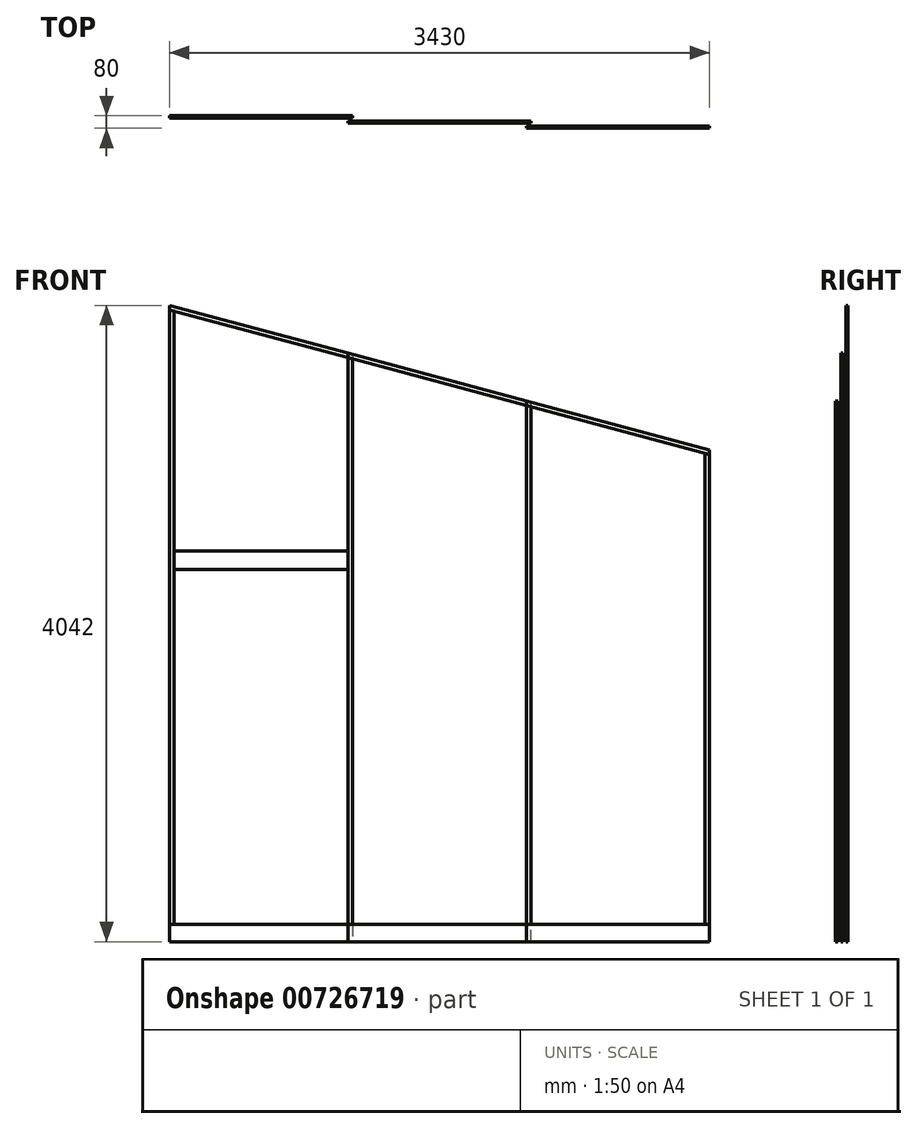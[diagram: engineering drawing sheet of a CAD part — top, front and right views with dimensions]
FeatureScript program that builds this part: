
annotation { "Feature Type Name" : "Feature", "Feature Type Description" : "" }
export const myFeature = defineFeature(function(context is Context, id is Id, definition is map)
    precondition{}
    {
        {
            assignVariable(context, id + "F0", {"name" : "bredd", "anyValue" : 28});
        }
        {
            var Q0;
            Q0=qCreatedBy(makeId("Front.planeOp"),FACE);
            var sketch = newSketch(context, id + "F1", { "sketchPlane" : qUnion([Q0])});
            skLineSegment(sketch, "E0", {"start": v(0, 0) * mm, "end": v(8388.04, 0) * mm});
            skLineSegment(sketch, "E1", {"start": v(8388.04, 0) * mm, "end": v(8388.04, 3249.78) * mm});
            skLineSegment(sketch, "E2", {"start": v(8388.04, 3249.78) * mm, "end": v(0, 5470.3) * mm});
            skLineSegment(sketch, "E3", {"start": v(0, 5470.3) * mm, "end": v(0, 0) * mm});
            skLineSegment(sketch, "E4", {"start": v(1277.9, 5132) * mm, "end": v(1277.9, 0) * mm, "construction": true});
            skLineSegment(sketch, "E5", {"start": v(4707.9, 4224) * mm, "end": v(4707.9, 0) * mm, "construction": true});
            skLineSegment(sketch, "E6", {"start": v(1277.9, 4042) * mm, "end": v(4707.9, 3124) * mm, "construction": true});
            skLineSegment(sketch, "E7", {"start": v(5395.42, 4042) * mm, "end": v(5395.42, 0) * mm, "construction": true});
            skSolve(sketch);
        }
        {
            var Q0;
            Q0=qCreatedBy(makeId("Front.planeOp"),FACE);
            var sketch = newSketch(context, id + "F2", { "sketchPlane" : qUnion([Q0])});
            skLineSegment(sketch, "E8.bottom", {"start": v(1277.9, 0) * mm, "end": v(1372.9, 0) * mm});
            skLineSegment(sketch, "E8.top", {"start": v(1277.9, 2328) * mm, "end": v(1372.9, 2328) * mm});
            skLineSegment(sketch, "E8.left", {"start": v(1277.9, 0) * mm, "end": v(1277.9, 2328) * mm});
            skLineSegment(sketch, "E8.right", {"start": v(1372.9, 0) * mm, "end": v(1372.9, 2328) * mm});
            skLineSegment(sketch, "E9.bottom", {"start": v(2372.9, 0) * mm, "end": v(2492.9, 0) * mm});
            skLineSegment(sketch, "E9.top", {"start": v(2372.9, 2328) * mm, "end": v(2492.9, 2328) * mm});
            skLineSegment(sketch, "E9.left", {"start": v(2372.9, 0) * mm, "end": v(2372.9, 2328) * mm});
            skLineSegment(sketch, "E9.right", {"start": v(2492.9, 0) * mm, "end": v(2492.9, 2328) * mm});
            skLineSegment(sketch, "E10.bottom", {"start": v(3492.9, 0) * mm, "end": v(3612.9, 0) * mm});
            skLineSegment(sketch, "E10.top", {"start": v(3492.9, 2328) * mm, "end": v(3612.9, 2328) * mm});
            skLineSegment(sketch, "E10.left", {"start": v(3492.9, 0) * mm, "end": v(3492.9, 2328) * mm});
            skLineSegment(sketch, "E10.right", {"start": v(3612.9, 0) * mm, "end": v(3612.9, 2328) * mm});
            skLineSegment(sketch, "E11", {"start": v(1277.9, 2328) * mm, "end": v(4707.9, 2328) * mm, "construction": true});
            skLineSegment(sketch, "E12.bottom", {"start": v(4707.9, 2328) * mm, "end": v(4612.9, 2328) * mm});
            skLineSegment(sketch, "E12.top", {"start": v(4707.9, 0) * mm, "end": v(4612.9, 0) * mm});
            skLineSegment(sketch, "E12.left", {"start": v(4707.9, 2328) * mm, "end": v(4707.9, 0) * mm});
            skLineSegment(sketch, "E12.right", {"start": v(4612.9, 2328) * mm, "end": v(4612.9, 0) * mm});
            skLineSegment(sketch, "E13.bottom", {"start": v(1262.9, 2328) * mm, "end": v(4722.9, 2328) * mm});
            skLineSegment(sketch, "E13.top", {"start": v(1262.9, 2423) * mm, "end": v(4722.9, 2423) * mm});
            skLineSegment(sketch, "E13.left", {"start": v(1262.9, 2328) * mm, "end": v(1262.9, 2423) * mm});
            skLineSegment(sketch, "E13.right", {"start": v(4722.9, 2328) * mm, "end": v(4722.9, 2423) * mm});
            skLineSegment(sketch, "E14.0", {"start": v(1277.9, 4042) * mm, "end": v(4707.9, 3124) * mm, "construction": true});
            skLineSegment(sketch, "E15", {"start": v(1262.9, 4046.01) * mm, "end": v(4722.9, 3119.99) * mm});
            skLineSegment(sketch, "E16", {"start": v(4722.9, 3119.99) * mm, "end": v(4722.9, 3021.64) * mm});
            skLineSegment(sketch, "E17", {"start": v(4722.9, 3021.64) * mm, "end": v(1262.9, 3947.67) * mm});
            skLineSegment(sketch, "E18", {"start": v(1262.9, 4046.01) * mm, "end": v(1262.9, 3947.67) * mm});
            skLineSegment(sketch, "E19", {"start": v(1262.9, 2423) * mm, "end": v(1262.9, 4046.01) * mm, "construction": true});
            skLineSegment(sketch, "E20", {"start": v(4722.9, 2423) * mm, "end": v(4722.9, 3119.99) * mm, "construction": true});
            skLineSegment(sketch, "E21.bottom", {"start": v(1277.9, 2483) * mm, "end": v(1372.9, 2483) * mm});
            skLineSegment(sketch, "E21.left", {"start": v(1277.9, 2483) * mm, "end": v(1277.9, 3943.66) * mm});
            skLineSegment(sketch, "E21.right", {"start": v(1372.9, 2483) * mm, "end": v(1372.9, 3918.23) * mm});
            skLineSegment(sketch, "E22.bottom", {"start": v(2372.9, 2483) * mm, "end": v(2492.9, 2483) * mm});
            skLineSegment(sketch, "E22.left", {"start": v(2372.9, 2483) * mm, "end": v(2372.9, 3650.6) * mm});
            skLineSegment(sketch, "E22.right", {"start": v(2492.9, 2483) * mm, "end": v(2492.9, 3618.48) * mm});
            skLineSegment(sketch, "E23.bottom", {"start": v(3492.9, 2483) * mm, "end": v(3612.9, 2483) * mm});
            skLineSegment(sketch, "E23.left", {"start": v(3492.9, 2483) * mm, "end": v(3492.9, 3350.84) * mm});
            skLineSegment(sketch, "E23.right", {"start": v(3612.9, 2483) * mm, "end": v(3612.9, 3318.72) * mm});
            skLineSegment(sketch, "E24.bottom", {"start": v(4612.9, 2483) * mm, "end": v(4707.9, 2483) * mm});
            skLineSegment(sketch, "E24.left", {"start": v(4612.9, 2483) * mm, "end": v(4612.9, 3051.08) * mm});
            skLineSegment(sketch, "E24.right", {"start": v(4707.9, 2483) * mm, "end": v(4707.9, 3025.66) * mm});
            skPoint(sketch, "E25.orphan", {"position": v(3612.9, 2483) * mm});
            skPoint(sketch, "E26.orphan", {"position": v(2492.9, 3618.48) * mm});
            skPoint(sketch, "E27.orphan", {"position": v(1372.9, 3918.23) * mm});
            skLineSegment(sketch, "E28", {"start": v(1372.9, 2571) * mm, "end": v(2372.9, 2571) * mm});
            skLineSegment(sketch, "E29", {"start": v(2492.9, 2571) * mm, "end": v(3492.9, 2571) * mm});
            skLineSegment(sketch, "E30", {"start": v(3612.9, 2571) * mm, "end": v(4612.9, 2571) * mm});
            skLineSegment(sketch, "E31", {"start": v(4612.9, 2498) * mm, "end": v(3612.9, 2498) * mm});
            skLineSegment(sketch, "E32", {"start": v(3492.9, 2498) * mm, "end": v(2492.9, 2498) * mm});
            skLineSegment(sketch, "E33", {"start": v(2372.9, 2498) * mm, "end": v(1372.9, 2498) * mm});
            skSolve(sketch);
        }
        {
            var Q0;
            Q0=qCreatedBy(makeId("Front.planeOp"),FACE);
            var sketch = newSketch(context, id + "F3", { "sketchPlane" : qUnion([Q0])});
            skPoint(sketch, "E34.0", {"position": v(1277.9, 0) * mm});
            skPoint(sketch, "E35.0", {"position": v(4707.9, 0) * mm});
            skPoint(sketch, "E36.0", {"position": v(4707.9, 3124) * mm});
            skPoint(sketch, "E37.0", {"position": v(1277.9, 4042) * mm});
            skLineSegment(sketch, "E38", {"start": v(1277.9, 0) * mm, "end": v(1277.9, 4042) * mm});
            skLineSegment(sketch, "E39", {"start": v(4707.9, 0) * mm, "end": v(4707.9, 3124) * mm});
            skLineSegment(sketch, "E40", {"start": v(1277.9, 0) * mm, "end": v(4707.9, 0) * mm, "construction": true});
            skLineSegment(sketch, "E41", {"start": v(2411.9, 110) * mm, "end": v(2411.9, 3709.51) * mm});
            skLineSegment(sketch, "E42", {"start": v(2439.9, 3731) * mm, "end": v(2439.9, 0) * mm});
            skLineSegment(sketch, "E43", {"start": v(3545.9, 3435) * mm, "end": v(3545.9, 0) * mm});
            skLineSegment(sketch, "E44", {"start": v(3573.9, 110) * mm, "end": v(3573.9, 3398.52) * mm});
            skLineSegment(sketch, "E45", {"start": v(2411.9, 0) * mm, "end": v(2439.9, 0) * mm});
            skLineSegment(sketch, "E46.bottom", {"start": v(1277.9, -203.85) * mm, "end": v(2439.9, -203.85) * mm, "construction": true});
            skLineSegment(sketch, "E46.top", {"start": v(1277.9, -239.4) * mm, "end": v(2439.9, -239.4) * mm, "construction": true});
            skLineSegment(sketch, "E46.left", {"start": v(1277.9, -203.85) * mm, "end": v(1277.9, -239.4) * mm, "construction": true});
            skLineSegment(sketch, "E46.right", {"start": v(2439.9, -203.85) * mm, "end": v(2439.9, -239.4) * mm, "construction": true});
            skLineSegment(sketch, "E47.bottom", {"start": v(2411.9, -167.17) * mm, "end": v(3573.9, -167.17) * mm, "construction": true});
            skLineSegment(sketch, "E47.top", {"start": v(2411.9, -203.85) * mm, "end": v(3573.9, -203.85) * mm, "construction": true});
            skLineSegment(sketch, "E47.left", {"start": v(2411.9, -167.17) * mm, "end": v(2411.9, -203.85) * mm, "construction": true});
            skLineSegment(sketch, "E47.right", {"start": v(3573.9, -167.17) * mm, "end": v(3573.9, -203.85) * mm, "construction": true});
            skLineSegment(sketch, "E48.bottom", {"start": v(4707.9, -203.85) * mm, "end": v(3545.9, -203.85) * mm, "construction": true});
            skLineSegment(sketch, "E48.top", {"start": v(4707.9, -239.4) * mm, "end": v(3545.9, -239.4) * mm, "construction": true});
            skLineSegment(sketch, "E48.left", {"start": v(4707.9, -203.85) * mm, "end": v(4707.9, -239.4) * mm, "construction": true});
            skLineSegment(sketch, "E48.right", {"start": v(3545.9, -203.85) * mm, "end": v(3545.9, -239.4) * mm, "construction": true});
            skLineSegment(sketch, "E49.0", {"start": v(1305.9, 110) * mm, "end": v(1305.9, 4005.52) * mm});
            skLineSegment(sketch, "E50.0", {"start": v(4679.9, 110) * mm, "end": v(4679.9, 3102.5) * mm});
            skLineSegment(sketch, "E51", {"start": v(4707.9, 3124) * mm, "end": v(3545.9, 3435) * mm});
            skLineSegment(sketch, "E52", {"start": v(1277.9, 4042) * mm, "end": v(2439.9, 3731) * mm});
            skLineSegment(sketch, "E53.0", {"start": v(1277.9, 4013.01) * mm, "end": v(2439.9, 3702.02) * mm});
            skLineSegment(sketch, "E54.0", {"start": v(4707.9, 3095.01) * mm, "end": v(3545.9, 3406.01) * mm});
            skLineSegment(sketch, "E55", {"start": v(1277.9, 4042) * mm, "end": v(4707.9, 3124) * mm, "construction": true});
            skLineSegment(sketch, "E56", {"start": v(1277.9, 0) * mm, "end": v(2439.9, 0) * mm});
            skLineSegment(sketch, "E57", {"start": v(2439.9, 110) * mm, "end": v(1277.9, 110) * mm});
            skLineSegment(sketch, "E58", {"start": v(3545.9, 0) * mm, "end": v(4707.9, 0) * mm});
            skLineSegment(sketch, "E59", {"start": v(3545.9, 110) * mm, "end": v(4707.9, 110) * mm});
            skPoint(sketch, "E60.orphan", {"position": v(3573.9, 0) * mm});
            skLineSegment(sketch, "E61.bottom", {"start": v(1305.9, 2483.58) * mm, "end": v(2411.9, 2483.58) * mm});
            skLineSegment(sketch, "E61.top", {"start": v(1305.9, 2363.58) * mm, "end": v(2411.9, 2363.58) * mm});
            skLineSegment(sketch, "E61.left", {"start": v(1305.9, 2483.58) * mm, "end": v(1305.9, 2363.58) * mm});
            skLineSegment(sketch, "E61.right", {"start": v(2411.9, 2483.58) * mm, "end": v(2411.9, 2363.58) * mm});
            skSolve(sketch);
        }
        {
            var Q0;
            Q0=qCreatedBy(makeId("Front.planeOp"),FACE);
            var sketch = newSketch(context, id + "F4", { "sketchPlane" : qUnion([Q0])});
            skLineSegment(sketch, "E62.0", {"start": v(2411.9, 110) * mm, "end": v(2411.9, 3709.51) * mm});
            skLineSegment(sketch, "E63.0", {"start": v(3573.9, 110) * mm, "end": v(3573.9, 3398.52) * mm});
            skLineSegment(sketch, "E64", {"start": v(2411.9, 110) * mm, "end": v(3573.9, 110) * mm});
            skLineSegment(sketch, "E65", {"start": v(3573.9, 3398.52) * mm, "end": v(2411.9, 3709.51) * mm});
            skLineSegment(sketch, "E66.0", {"start": v(3545.9, 110) * mm, "end": v(3545.9, 3406.01) * mm});
            skLineSegment(sketch, "E66.2", {"start": v(2439.9, 110) * mm, "end": v(2439.9, 3702.02) * mm});
            skLineSegment(sketch, "E67", {"start": v(2411.9, 110) * mm, "end": v(2411.9, 0) * mm});
            skLineSegment(sketch, "E68", {"start": v(2411.9, 0) * mm, "end": v(3573.9, 0) * mm});
            skLineSegment(sketch, "E69", {"start": v(3573.9, 0) * mm, "end": v(3573.9, 110) * mm});
            skLineSegment(sketch, "E70.0", {"start": v(3573.9, 3427.5) * mm, "end": v(2411.9, 3738.5) * mm});
            skLineSegment(sketch, "E71", {"start": v(3573.9, 3398.52) * mm, "end": v(3573.9, 3427.5) * mm});
            skLineSegment(sketch, "E72", {"start": v(2411.9, 3709.51) * mm, "end": v(2411.9, 3738.5) * mm});
            skSolve(sketch);
        }
        {
            var Q0;
            {var subQ4=sQuery(id+"F3.wireOp",EDGE,"E52");Q0=makeQuery(id+"F3.imprint","IMPRINT",FACE,{"disambiguationData":[TD([[makeQuery(id+"F3.imprint","IMPRINT",EDGE,{"derivedFrom":subQ4}),-1.0]])]});}
            extrude(context, id + "F5", {"entities" : qUnion([Q0]), "depth" : (getVariable(context, 'bredd') / 2) * mm, "offsetDistance" : 25 * mm});
        }
        {
            var Q0;
            {var subQ0=sQuery(id+"F3.wireOp",EDGE,"E41");Q0=makeQuery(id+"F3.imprint","IMPRINT",FACE,{"disambiguationData":[TD([[makeQuery(id+"F3.imprint","IMPRINT",EDGE,{"derivedFrom":subQ0}),-1.0]])]});}
            extrude(context, id + "F6", {"entities" : qUnion([Q0]), "depth" : (getVariable(context, 'bredd') / 2) * mm, "offsetDistance" : 25 * mm});
        }
        {
            var Q0;
            {var subQ5=sQuery(id+"F3.wireOp",EDGE,"E49.0");Q0=makeQuery(id+"F3.imprint","IMPRINT",FACE,{"disambiguationData":[TD([[makeQuery(id+"F3.imprint","IMPRINT",EDGE,{"derivedFrom":subQ5}),1.0]])]});}
            extrude(context, id + "F7", {"entities" : qUnion([Q0]), "depth" : (getVariable(context, 'bredd') / 2) * mm, "offsetDistance" : 25 * mm});
        }
        {
            var Q0;
            {var subQ0=sQuery(id+"F3.wireOp",EDGE,"E56");var subQ1=sQuery(id+"F3.wireOp",EDGE,"E38");var subQ2=makeQuery(id+"F3.imprint","INTERSECT",VERTEX,{"derivedFrom":[subQ1,subQ0]});Q0=makeQuery(id+"F3.imprint","IMPRINT",FACE,{"disambiguationData":[TD([[makeQuery(id+"F3.imprint","IMPRINT",EDGE,{"disambiguationData":[TD([[subQ2,-1.0]])],"derivedFrom":subQ1}),-1.0]])]});}
            extrude(context, id + "F8", {"entities" : qUnion([Q0]), "depth" : (getVariable(context, 'bredd') / 2) * mm, "offsetDistance" : 25 * mm});
        }
        {
            var Q0;
            Q0=makeQuery(id+"F4.imprint","IMPRINT",FACE,{"disambiguationData":[TD([[makeQuery(id+"F4.imprint","IMPRINT",EDGE,{"derivedFrom":sQuery(id+"F4.wireOp",EDGE,"E70.0")}),1.0]])]});
            extrude(context, id + "F9", {"entities" : qUnion([Q0]), "depth" : (getVariable(context, 'bredd') + 5 + getVariable(context, 'bredd') / 2) * mm, "offsetDistance" : 25 * mm, "hasSecondDirection" : true, "secondDirectionOppositeDirection" : false, "secondDirectionDepth" : (getVariable(context, 'bredd') + 5) * mm});
        }
        {
            var Q0;
            {var subQ0=sQuery(id+"F4.wireOp",EDGE,"E62.0");Q0=makeQuery(id+"F4.imprint","IMPRINT",FACE,{"disambiguationData":[TD([[makeQuery(id+"F4.imprint","IMPRINT",EDGE,{"derivedFrom":subQ0}),-1.0]])]});}
            extrude(context, id + "F10", {"entities" : qUnion([Q0]), "depth" : (getVariable(context, 'bredd') + 5 + getVariable(context, 'bredd') / 2) * mm, "offsetDistance" : 25 * mm, "hasSecondDirection" : true, "secondDirectionOppositeDirection" : false, "secondDirectionDepth" : (getVariable(context, 'bredd') + 5) * mm});
        }
        {
            var Q0;
            {var subQ0=sQuery(id+"F4.wireOp",EDGE,"E63.0");Q0=makeQuery(id+"F4.imprint","IMPRINT",FACE,{"disambiguationData":[TD([[makeQuery(id+"F4.imprint","IMPRINT",EDGE,{"derivedFrom":subQ0}),1.0]])]});}
            extrude(context, id + "F11", {"entities" : qUnion([Q0]), "depth" : (getVariable(context, 'bredd') + 5 + getVariable(context, 'bredd') / 2) * mm, "offsetDistance" : 25 * mm, "hasSecondDirection" : true, "secondDirectionOppositeDirection" : false, "secondDirectionDepth" : (getVariable(context, 'bredd') + 5) * mm});
        }
        {
            var Q0;
            {var subQ0=sQuery(id+"F4.wireOp",EDGE,"E67");Q0=makeQuery(id+"F4.imprint","IMPRINT",FACE,{"disambiguationData":[TD([[makeQuery(id+"F4.imprint","IMPRINT",EDGE,{"derivedFrom":subQ0}),1.0]])]});}
            extrude(context, id + "F12", {"entities" : qUnion([Q0]), "depth" : (getVariable(context, 'bredd') + 5 + getVariable(context, 'bredd') / 2) * mm, "offsetDistance" : 25 * mm, "hasSecondDirection" : true, "secondDirectionOppositeDirection" : false, "secondDirectionDepth" : (getVariable(context, 'bredd') + 5) * mm});
        }
        {
            var Q0;
            {var subQ4=sQuery(id+"F3.wireOp",EDGE,"E51");Q0=makeQuery(id+"F3.imprint","IMPRINT",FACE,{"disambiguationData":[TD([[makeQuery(id+"F3.imprint","IMPRINT",EDGE,{"derivedFrom":subQ4}),1.0]])]});}
            extrude(context, id + "F13", {"entities" : qUnion([Q0]), "depth" : (getVariable(context, 'bredd') * 2 + 10 + getVariable(context, 'bredd') / 2) * mm, "offsetDistance" : 25 * mm, "hasSecondDirection" : true, "secondDirectionOppositeDirection" : false, "secondDirectionDepth" : (getVariable(context, 'bredd') * 2 + 10) * mm});
        }
        {
            var Q0;
            {var subQ5=sQuery(id+"F3.wireOp",EDGE,"E44");Q0=makeQuery(id+"F3.imprint","IMPRINT",FACE,{"disambiguationData":[TD([[makeQuery(id+"F3.imprint","IMPRINT",EDGE,{"derivedFrom":subQ5}),1.0]])]});}
            extrude(context, id + "F14", {"entities" : qUnion([Q0]), "depth" : (getVariable(context, 'bredd') * 2 + 10 + getVariable(context, 'bredd') / 2) * mm, "offsetDistance" : 25 * mm, "hasSecondDirection" : true, "secondDirectionOppositeDirection" : false, "secondDirectionDepth" : (getVariable(context, 'bredd') * 2 + 10) * mm});
        }
        {
            var Q0;
            {var subQ5=sQuery(id+"F3.wireOp",EDGE,"E50.0");Q0=makeQuery(id+"F3.imprint","IMPRINT",FACE,{"disambiguationData":[TD([[makeQuery(id+"F3.imprint","IMPRINT",EDGE,{"derivedFrom":subQ5}),-1.0]])]});}
            extrude(context, id + "F15", {"entities" : qUnion([Q0]), "depth" : (getVariable(context, 'bredd') * 2 + 10 + getVariable(context, 'bredd') / 2) * mm, "offsetDistance" : 25 * mm, "hasSecondDirection" : true, "secondDirectionOppositeDirection" : false, "secondDirectionDepth" : (getVariable(context, 'bredd') * 2 + 10) * mm});
        }
        {
            var Q0;
            {var subQ4=sQuery(id+"F3.wireOp",EDGE,"E58");Q0=makeQuery(id+"F3.imprint","IMPRINT",FACE,{"disambiguationData":[TD([[makeQuery(id+"F3.imprint","IMPRINT",EDGE,{"derivedFrom":subQ4}),1.0]])]});}
            extrude(context, id + "F16", {"entities" : qUnion([Q0]), "depth" : (getVariable(context, 'bredd') * 2 + 10 + getVariable(context, 'bredd') / 2) * mm, "offsetDistance" : 25 * mm, "hasSecondDirection" : true, "secondDirectionOppositeDirection" : false, "secondDirectionDepth" : (getVariable(context, 'bredd') * 2 + 10) * mm});
        }
        {
            var Q0;
            Q0=makeQuery(id+"F3.imprint","IMPRINT",FACE,{"disambiguationData":[TD([[makeQuery(id+"F3.imprint","IMPRINT",EDGE,{"derivedFrom":sQuery(id+"F3.wireOp",EDGE,"E61.bottom")}),-1.0]])]});
            extrude(context, id + "F17", {"entities" : qUnion([Q0]), "depth" : (getVariable(context, 'bredd') / 2) * mm, "offsetDistance" : 25 * mm});
        }
    });
